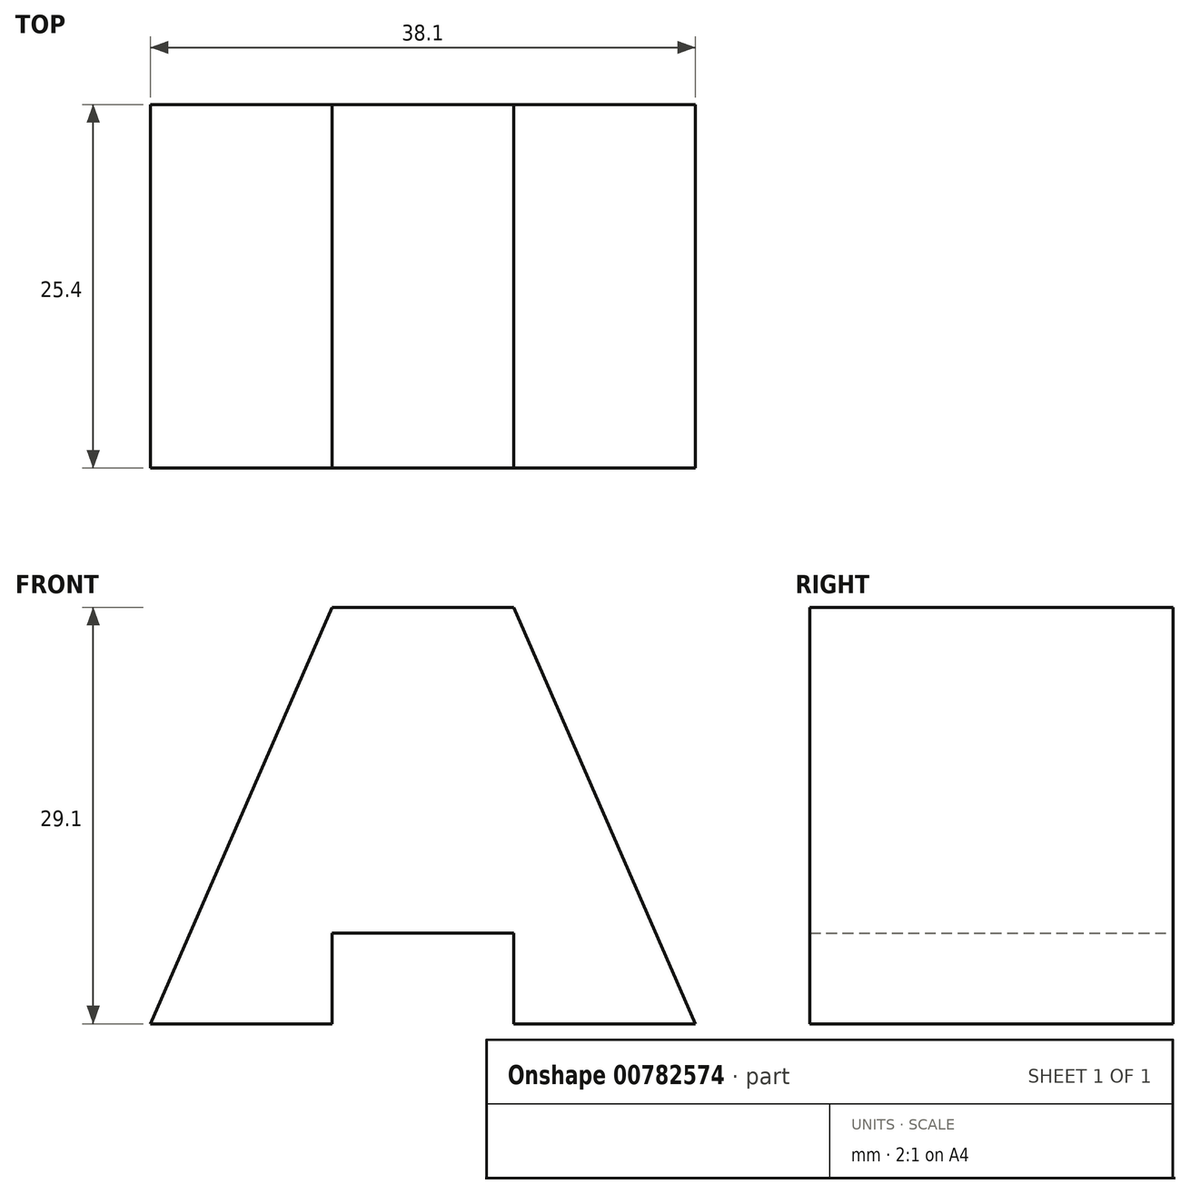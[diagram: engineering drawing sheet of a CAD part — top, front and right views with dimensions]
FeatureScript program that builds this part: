
annotation { "Feature Type Name" : "Feature", "Feature Type Description" : "" }
export const myFeature = defineFeature(function(context is Context, id is Id, definition is map)
    precondition{}
    {
        {
            var Q0;
            Q0=qCreatedBy(makeId("Front.planeOp"),FACE);
            var sketch = newSketch(context, id + "F0", { "sketchPlane" : qUnion([Q0])});
            skLineSegment(sketch, "E0", {"start": v(12.7, 0) * mm, "end": v(0, 0) * mm});
            skLineSegment(sketch, "E1", {"start": v(0, 0) * mm, "end": v(12.7, 29.1) * mm});
            skLineSegment(sketch, "E2", {"start": v(12.7, 29.1) * mm, "end": v(25.4, 29.1) * mm});
            skLineSegment(sketch, "E3", {"start": v(12.7, 0) * mm, "end": v(12.7, 6.35) * mm});
            skLineSegment(sketch, "E4", {"start": v(12.7, 6.35) * mm, "end": v(25.4, 6.35) * mm});
            skLineSegment(sketch, "E5", {"start": v(25.4, 6.35) * mm, "end": v(25.4, 0) * mm});
            skLineSegment(sketch, "E6", {"start": v(25.4, 0) * mm, "end": v(38.1, 0) * mm});
            skLineSegment(sketch, "E7", {"start": v(38.1, 0) * mm, "end": v(25.4, 29.1) * mm});
            skSolve(sketch);
        }
        {
            var Q0;
            Q0=makeQuery(id+"F0.imprint","IMPRINT",FACE,{"disambiguationData":[TD([[makeQuery(id+"F0.imprint","IMPRINT",EDGE,{"derivedFrom":sQuery(id+"F0.wireOp",EDGE,"E0")}),-1.0]])]});
            extrude(context, id + "F1", {"entities" : qUnion([Q0]), "depth" : 25.4 * mm, "offsetDistance" : 25.4 * mm});
        }
    });
